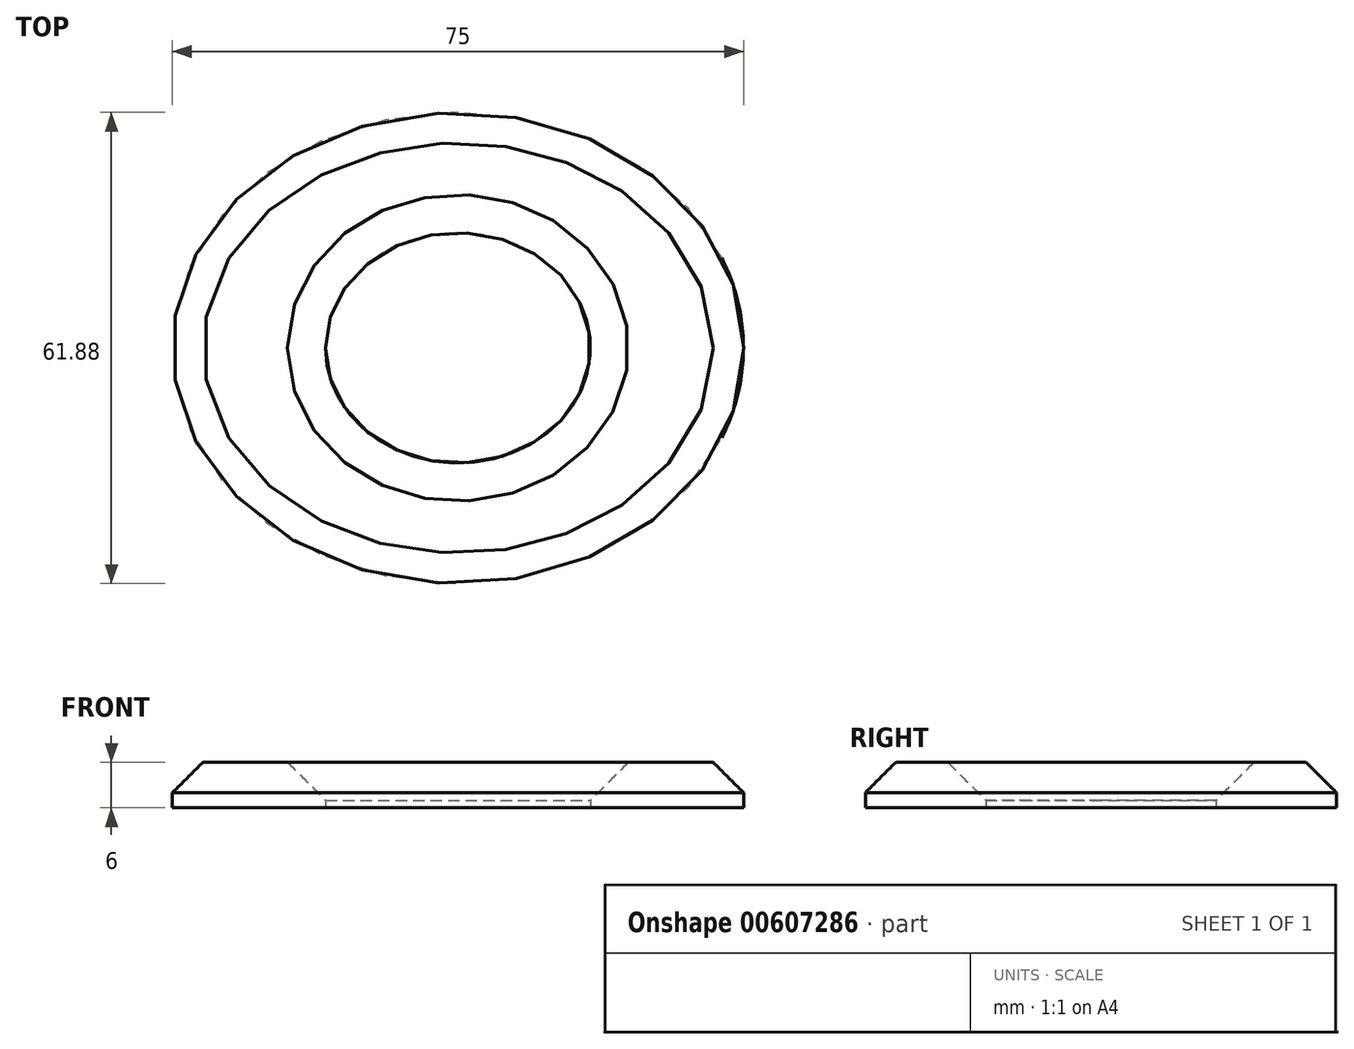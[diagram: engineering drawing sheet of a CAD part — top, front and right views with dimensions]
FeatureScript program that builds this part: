
annotation { "Feature Type Name" : "Feature", "Feature Type Description" : "" }
export const myFeature = defineFeature(function(context is Context, id is Id, definition is map)
    precondition{}
    {
        {
            var Q0;
            Q0=qCreatedBy(makeId("Top.planeOp"),FACE);
            var sketch = newSketch(context, id + "F0", { "sketchPlane" : qUnion([Q0])});
            skEllipse(sketch, "E0", {"center": v(0, 0) * mm, "majorRadius": 37.5 * mm, "minorRadius": 30.94 * mm, "majorAxis": v(1, 0)});
            skEllipse(sketch, "E1", {"center": v(0, 0) * mm, "majorRadius": 15.13 * mm, "minorRadius": 17.4 * mm, "majorAxis": v(0, 1)});
            skSolve(sketch);
        }
        {
            var Q0;
            Q0=makeQuery(id+"F0.imprint","IMPRINT",FACE,{"disambiguationData":[TD([[makeQuery(id+"F0.imprint","IMPRINT",EDGE,{"derivedFrom":sQuery(id+"F0.wireOp",EDGE,"E0")}),1.0]])]});
            extrude(context, id + "F1", {"entities" : qUnion([Q0]), "depth" : 6 * mm, "offsetDistance" : 25 * mm});
        }
        {
            var Q0;
            Q0=makeQuery(id+"F1.opExtrude","CAP_EDGE",EDGE,{"disambiguationData":[OSD([sQuery(id+"F0.wireOp",EDGE,"E1")])],"isStart":false});
            chamfer(context, id + "F2", {"entities" : qUnion([Q0]), "chamferType" : ChamferType.TWO_OFFSETS, "width1" : 5 * mm, "oppositeDirection" : false, "width2" : 5 * mm, "tangentPropagation" : true});
        }
        {
            var Q0;
            Q0=makeQuery(id+"F1.opExtrude","CAP_EDGE",EDGE,{"disambiguationData":[OSD([sQuery(id+"F0.wireOp",EDGE,"E0")])],"isStart":false});
            chamfer(context, id + "F3", {"entities" : qUnion([Q0]), "chamferType" : ChamferType.TWO_OFFSETS, "width1" : 4 * mm, "oppositeDirection" : false, "width2" : 4 * mm, "tangentPropagation" : true});
        }
    });
